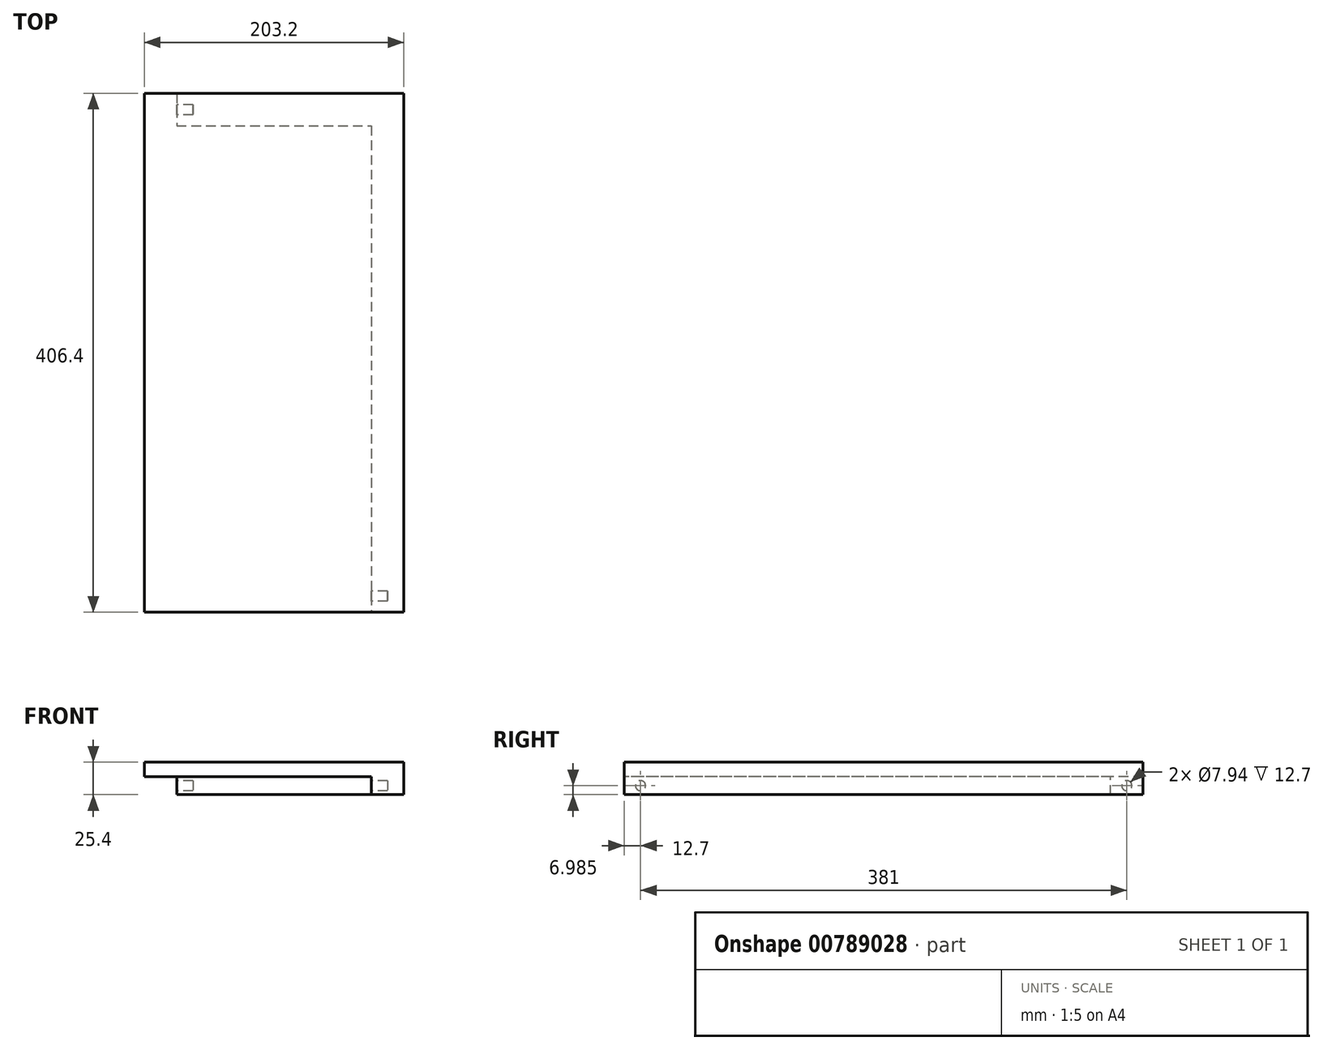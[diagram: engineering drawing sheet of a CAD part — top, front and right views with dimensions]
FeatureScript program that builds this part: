
annotation { "Feature Type Name" : "Feature", "Feature Type Description" : "" }
export const myFeature = defineFeature(function(context is Context, id is Id, definition is map)
    precondition{}
    {
        {
            var Q0;
            Q0=qCreatedBy(makeId("Top.planeOp"),FACE);
            var sketch = newSketch(context, id + "F0", { "sketchPlane" : qUnion([Q0])});
            skLineSegment(sketch, "E0.bottom", {"start": v(101.6, 203.2) * mm, "end": v(-101.6, 203.2) * mm});
            skLineSegment(sketch, "E0.top", {"start": v(101.6, -203.2) * mm, "end": v(-101.6, -203.2) * mm});
            skLineSegment(sketch, "E0.left", {"start": v(101.6, 203.2) * mm, "end": v(101.6, -203.2) * mm});
            skLineSegment(sketch, "E0.right", {"start": v(-101.6, 203.2) * mm, "end": v(-101.6, -203.2) * mm});
            skPoint(sketch, "E0.middle", {"position": v(0, 0) * mm});
            skLineSegment(sketch, "E1", {"start": v(-101.6, 177.8) * mm, "end": v(101.6, 177.8) * mm});
            skLineSegment(sketch, "E2", {"start": v(76.2, 203.2) * mm, "end": v(76.2, -203.2) * mm});
            skLineSegment(sketch, "E3", {"start": v(-76.2, 203.2) * mm, "end": v(-76.2, 177.8) * mm});
            skSolve(sketch);
        }
        {
            var Q0;
            {var subQ0=sQuery(id+"F0.wireOp",EDGE,"E0.left");var subQ1=sQuery(id+"F0.wireOp",EDGE,"E0.bottom");var subQ2=makeQuery(id+"F0.imprint","INTERSECT",VERTEX,{"derivedFrom":[subQ1,subQ0]});Q0=makeQuery(id+"F0.imprint","IMPRINT",FACE,{"disambiguationData":[TD([[makeQuery(id+"F0.imprint","IMPRINT",EDGE,{"disambiguationData":[TD([[subQ2,-1.0]])],"derivedFrom":subQ1}),1.0]])]});}
            var Q1;
            {var subQ0=sQuery(id+"F0.wireOp",EDGE,"E0.left");var subQ1=sQuery(id+"F0.wireOp",EDGE,"E0.top");var subQ2=makeQuery(id+"F0.imprint","INTERSECT",VERTEX,{"derivedFrom":[subQ1,subQ0]});Q1=makeQuery(id+"F0.imprint","IMPRINT",FACE,{"disambiguationData":[TD([[makeQuery(id+"F0.imprint","IMPRINT",EDGE,{"disambiguationData":[TD([[subQ2,-1.0]])],"derivedFrom":subQ1}),-1.0]])]});}
            var Q2;
            {var subQ3=sQuery(id+"F0.wireOp",EDGE,"E3");Q2=makeQuery(id+"F0.imprint","IMPRINT",FACE,{"disambiguationData":[TD([[makeQuery(id+"F0.imprint","IMPRINT",EDGE,{"derivedFrom":subQ3}),1.0]])]});}
            extrude(context, id + "F1", {"entities" : qUnion([Q0, Q1, Q2]), "oppositeDirection" : true, "depth" : 25.4 * mm, "offsetDistance" : 25.4 * mm});
        }
        {
            var Q0;
            {var subQ0=sQuery(id+"F0.wireOp",EDGE,"E0.right");var subQ1=sQuery(id+"F0.wireOp",EDGE,"E0.top");var subQ2=makeQuery(id+"F0.imprint","INTERSECT",VERTEX,{"derivedFrom":[subQ1,subQ0]});Q0=makeQuery(id+"F0.imprint","IMPRINT",FACE,{"disambiguationData":[TD([[makeQuery(id+"F0.imprint","IMPRINT",EDGE,{"disambiguationData":[TD([[subQ2,1.0]])],"derivedFrom":subQ1}),-1.0]])]});}
            var Q1;
            {var subQ3=sQuery(id+"F0.wireOp",EDGE,"E3");Q1=makeQuery(id+"F0.imprint","IMPRINT",FACE,{"disambiguationData":[TD([[makeQuery(id+"F0.imprint","IMPRINT",EDGE,{"derivedFrom":subQ3}),-1.0]])]});}
            extrude(context, id + "F2", {"entities" : qUnion([Q0, Q1]), "operationType" : NewBodyOperationType.ADD, "oppositeDirection" : true, "depth" : 11.43 * mm, "offsetDistance" : 25.4 * mm});
        }
        {
            var Q0;
            Q0=makeQuery(id+"F1.opExtrude","SWEPT_FACE",FACE,{"disambiguationData":[OSD([sQuery(id+"F0.wireOp",EDGE,"E3")])]});
            var sketch = newSketch(context, id + "F3", { "sketchPlane" : qUnion([Q0])});
            skCircle(sketch, "E4", {"center": v(-190.5, -18.42) * mm, "radius": 3.97 * mm});
            skPoint(sketch, "E4.centerSnap0", {"position": v(-190.5, -11.43) * mm});
            skSolve(sketch);
        }
        {
            var Q0;
            Q0=makeQuery(id+"F3.imprint","IMPRINT",FACE,{"disambiguationData":[TD([[makeQuery(id+"F3.imprint","IMPRINT",EDGE,{"derivedFrom":sQuery(id+"F3.wireOp",EDGE,"E4")}),1.0]])]});
            extrude(context, id + "F4", {"entities" : qUnion([Q0]), "operationType" : NewBodyOperationType.REMOVE, "oppositeDirection" : true, "depth" : 12.7 * mm, "offsetDistance" : 25.4 * mm});
        }
        {
            var Q0;
            Q0=makeQuery(id+"F1.opExtrude","SWEPT_FACE",FACE,{"disambiguationData":[OSD([sQuery(id+"F0.wireOp",EDGE,"E2")])]});
            var sketch = newSketch(context, id + "F5", { "sketchPlane" : qUnion([Q0])});
            skCircle(sketch, "E5", {"center": v(190.5, -18.41) * mm, "radius": 3.97 * mm});
            skPoint(sketch, "E5.centerSnap0", {"position": v(203.2, -18.42) * mm});
            skSolve(sketch);
        }
        {
            var Q0;
            Q0=makeQuery(id+"F5.imprint","IMPRINT",FACE,{"disambiguationData":[TD([[makeQuery(id+"F5.imprint","IMPRINT",EDGE,{"derivedFrom":sQuery(id+"F5.wireOp",EDGE,"E5")}),1.0]])]});
            extrude(context, id + "F6", {"entities" : qUnion([Q0]), "operationType" : NewBodyOperationType.REMOVE, "oppositeDirection" : true, "depth" : 12.7 * mm, "offsetDistance" : 25.4 * mm});
        }
    });
